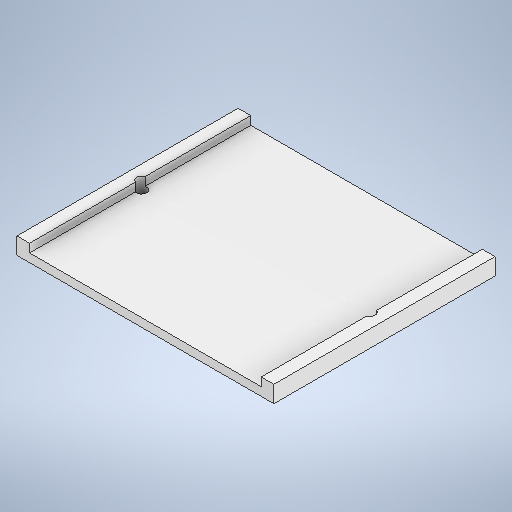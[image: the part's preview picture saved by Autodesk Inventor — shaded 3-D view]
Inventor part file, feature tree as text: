
AUTODESK INVENTOR PART (.ipt)
format: ipt  version: 2025 (Build 290162000, 162)  size: 257,024 bytes
history: native  units: in
note: dims shown in document units (in); Inventor stores cm internally (conversion verified against a paired STEP export)
features: sketch x3, extrude x2, hole x1
ambient origin geometry x8: Origin, YZ Plane, XZ Plane, XY Plane, X Axis, Y Axis, Z Axis, Center Point
bodies: Solid1 (feature_tree)
feature tree (6):
  extrude  "Extrusion1"  Depth=2.4016in
  extrude  "Extrusion2"  Depth=0.0787in TaperAngle=0.0deg
  hole  "Hole2"  [1 undecoded]
  sketch  "Sketch1"  dims[d0=2.0669in d1=2.4016in]
  sketch  "Sketch2"  dims[d2=0.1575in d3=0.0in d5=0.0787in d6=0.0in]
  sketch  "Sketch4"  dims[d19=0.0945in d20=0.2362in d21=0.1181in d22=0.0787in d23=90.0deg d24=0.315in d25=0.8108in d26=0.1181in d28=0.1319in d29=0.1181in d30=0.1319in]
note: 1 required parameter value undecoded (feature->parameter linkage not recoverable at this tier; creation-order binding heuristic only, values carry confidence <= 0.55)
